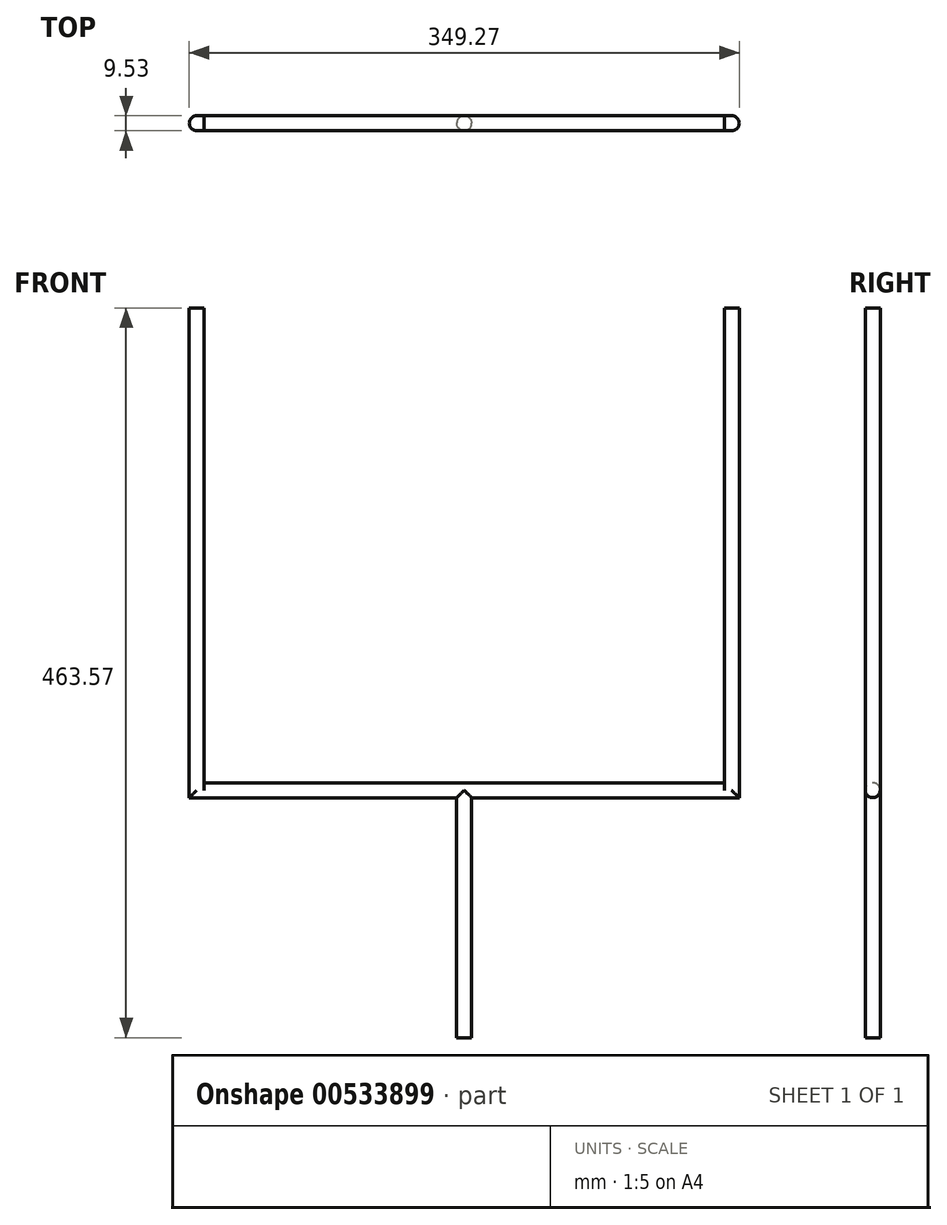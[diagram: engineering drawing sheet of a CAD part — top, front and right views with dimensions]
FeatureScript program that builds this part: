
annotation { "Feature Type Name" : "Feature", "Feature Type Description" : "" }
export const myFeature = defineFeature(function(context is Context, id is Id, definition is map)
    precondition{}
    {
        {
            var Q0;
            Q0=qCreatedBy(makeId("Front.planeOp"),FACE);
            var sketch = newSketch(context, id + "F0", { "sketchPlane" : qUnion([Q0])});
            skLineSegment(sketch, "E0", {"start": v(-9.35, -58.84) * mm, "end": v(-4.59, -58.84) * mm});
            skLineSegment(sketch, "E1", {"start": v(-9.35, -58.84) * mm, "end": v(-9.35, 93.58) * mm});
            skLineSegment(sketch, "E2", {"start": v(-4.59, 103.1) * mm, "end": v(-169.7, 103.1) * mm});
            skLineSegment(sketch, "E3", {"start": v(-169.7, 103.1) * mm, "end": v(-169.7, 404.73) * mm});
            skLineSegment(sketch, "E4", {"start": v(-169.7, 404.73) * mm, "end": v(-179.22, 404.73) * mm});
            skLineSegment(sketch, "E5", {"start": v(-179.22, 404.73) * mm, "end": v(-179.22, 93.58) * mm});
            skLineSegment(sketch, "E6", {"start": v(-9.35, 93.58) * mm, "end": v(-179.22, 93.58) * mm});
            skLineSegment(sketch, "E7.MirrorCS", {"start": v(-4.59, 103.1) * mm, "end": v(160.53, 103.1) * mm});
            skLineSegment(sketch, "E8.MirrorCS", {"start": v(0.17, 93.58) * mm, "end": v(170.05, 93.58) * mm});
            skLineSegment(sketch, "E9.MirrorCS", {"start": v(0.17, -58.84) * mm, "end": v(0.17, 93.58) * mm});
            skLineSegment(sketch, "E10.MirrorCS", {"start": v(0.17, -58.84) * mm, "end": v(-4.59, -58.84) * mm});
            skLineSegment(sketch, "E11.MirrorCS", {"start": v(170.05, 404.73) * mm, "end": v(170.05, 93.58) * mm});
            skLineSegment(sketch, "E12.MirrorCS", {"start": v(160.53, 103.1) * mm, "end": v(160.53, 404.73) * mm});
            skLineSegment(sketch, "E13.MirrorCS", {"start": v(160.53, 404.73) * mm, "end": v(170.05, 404.73) * mm});
            skPoint(sketch, "E14.end.orphan", {"position": v(-4.59, 93.58) * mm});
            skSolve(sketch);
        }
        {
            var Q0;
            Q0 = qSketchRegion(id + "F0", true);
            extrude(context, id + "F1", {"entities" : qUnion([Q0]), "depth" : 9.52 * mm, "offsetDistance" : 25.4 * mm});
        }
        {
            var Q0;
            Q0=makeQuery(id+"F1.opExtrude","CAP_EDGE",EDGE,{"disambiguationData":[OSD([sQuery(id+"F0.wireOp",EDGE,"E11.MirrorCS")])],"isStart":false});
            var Q1;
            Q1=makeQuery(id+"F1.opExtrude","CAP_EDGE",EDGE,{"disambiguationData":[OSD([sQuery(id+"F0.wireOp",EDGE,"E11.MirrorCS")])],"isStart":true});
            var Q2;
            Q2=makeQuery(id+"F1.opExtrude","CAP_EDGE",EDGE,{"disambiguationData":[OSD([sQuery(id+"F0.wireOp",EDGE,"E2"),sQuery(id+"F0.wireOp",EDGE,"E7.MirrorCS")])],"isStart":true});
            var Q3;
            Q3=makeQuery(id+"F1.opExtrude","CAP_EDGE",EDGE,{"disambiguationData":[OSD([sQuery(id+"F0.wireOp",EDGE,"E2"),sQuery(id+"F0.wireOp",EDGE,"E7.MirrorCS")])],"isStart":false});
            var Q4;
            Q4=makeQuery(id+"F1.opExtrude","CAP_EDGE",EDGE,{"disambiguationData":[OSD([sQuery(id+"F0.wireOp",EDGE,"E6")])],"isStart":false});
            var Q5;
            Q5=makeQuery(id+"F1.opExtrude","CAP_EDGE",EDGE,{"disambiguationData":[OSD([sQuery(id+"F0.wireOp",EDGE,"E6")])],"isStart":true});
            var Q6;
            Q6=makeQuery(id+"F1.opExtrude","CAP_EDGE",EDGE,{"disambiguationData":[OSD([sQuery(id+"F0.wireOp",EDGE,"E8.MirrorCS")])],"isStart":false});
            var Q7;
            Q7=makeQuery(id+"F1.opExtrude","CAP_EDGE",EDGE,{"disambiguationData":[OSD([sQuery(id+"F0.wireOp",EDGE,"E8.MirrorCS")])],"isStart":true});
            var Q8;
            Q8=makeQuery(id+"F1.opExtrude","CAP_EDGE",EDGE,{"disambiguationData":[OSD([sQuery(id+"F0.wireOp",EDGE,"E9.MirrorCS")])],"isStart":false});
            var Q9;
            Q9=makeQuery(id+"F1.opExtrude","CAP_EDGE",EDGE,{"disambiguationData":[OSD([sQuery(id+"F0.wireOp",EDGE,"E1")])],"isStart":false});
            var Q10;
            Q10=makeQuery(id+"F1.opExtrude","CAP_EDGE",EDGE,{"disambiguationData":[OSD([sQuery(id+"F0.wireOp",EDGE,"E1")])],"isStart":true});
            var Q11;
            Q11=makeQuery(id+"F1.opExtrude","CAP_EDGE",EDGE,{"disambiguationData":[OSD([sQuery(id+"F0.wireOp",EDGE,"E9.MirrorCS")])],"isStart":true});
            var Q12;
            Q12=makeQuery(id+"F1.opExtrude","CAP_EDGE",EDGE,{"disambiguationData":[OSD([sQuery(id+"F0.wireOp",EDGE,"E5")])],"isStart":true});
            var Q13;
            Q13=makeQuery(id+"F1.opExtrude","CAP_EDGE",EDGE,{"disambiguationData":[OSD([sQuery(id+"F0.wireOp",EDGE,"E5")])],"isStart":false});
            fillet(context, id + "F2", {"entities" : qUnion([Q0, Q1, Q2, Q3, Q4, Q5, Q6, Q7, Q8, Q9, Q10, Q11, Q12, Q13]), "radius" : 4.76 * mm, "tangentPropagation" : true, "allowEdgeOverflow" : false});
        }
    });
